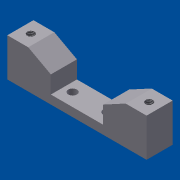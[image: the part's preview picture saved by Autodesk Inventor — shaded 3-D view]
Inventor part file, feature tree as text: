
AUTODESK INVENTOR PART (.ipt)
format: ipt  version: 2012 SP1 (Build 160190100, 190)  size: 113,664 bytes
history: native  units: in
note: dims shown in document units (in); Inventor stores cm internally (conversion verified against a paired STEP export)
features: sketch x3, extrude x2, hole x1, projected_geometry x1
ambient origin geometry x8: Origin, YZ Plane, XZ Plane, XY Plane, X Axis, Y Axis, Z Axis, Center Point
bodies: Solid1 (feature_tree)
feature tree (7):
  extrude  "Extrusion1"  Depth=3.1496in
  extrude  "Extrusion2"  Depth=0.4724in
  hole  "Hole1"  [1 undecoded]
  sketch  "Sketch1"  dims[d0=0.8661in d1=3.1496in]
  sketch  "Sketch2"  dims[d2=90.0deg d3=0.4724in]
  sketch  "Sketch3"  dims[d4=90.0deg d5=0.4724in d6=0.9843in d7=2.1654in d8=0.8661in d9=0.5906in d10=0.5906in d11=0.1969in d12=0.5906in d13=0.0in d14=0.1969in d15=0.7874in d17=0.7874in d18=0.3937in d20=0.3937in d22=1.1811in d23=0.2953in d24=0.5118in d25=0.0in d26=0.1969in d27=0.2953in d28=0.2362in d29=0.1969in d30=0.2362in d31=0.2953in d32=0.1628in d33=0.2362in d34=0.1575in d35=0.0787in d36=90.0deg d37=0.315in d38=0.8108in]
  projected_geometry  "Projected Loop1"
note: 1 required parameter value undecoded (feature->parameter linkage not recoverable at this tier; creation-order binding heuristic only, values carry confidence <= 0.55)
